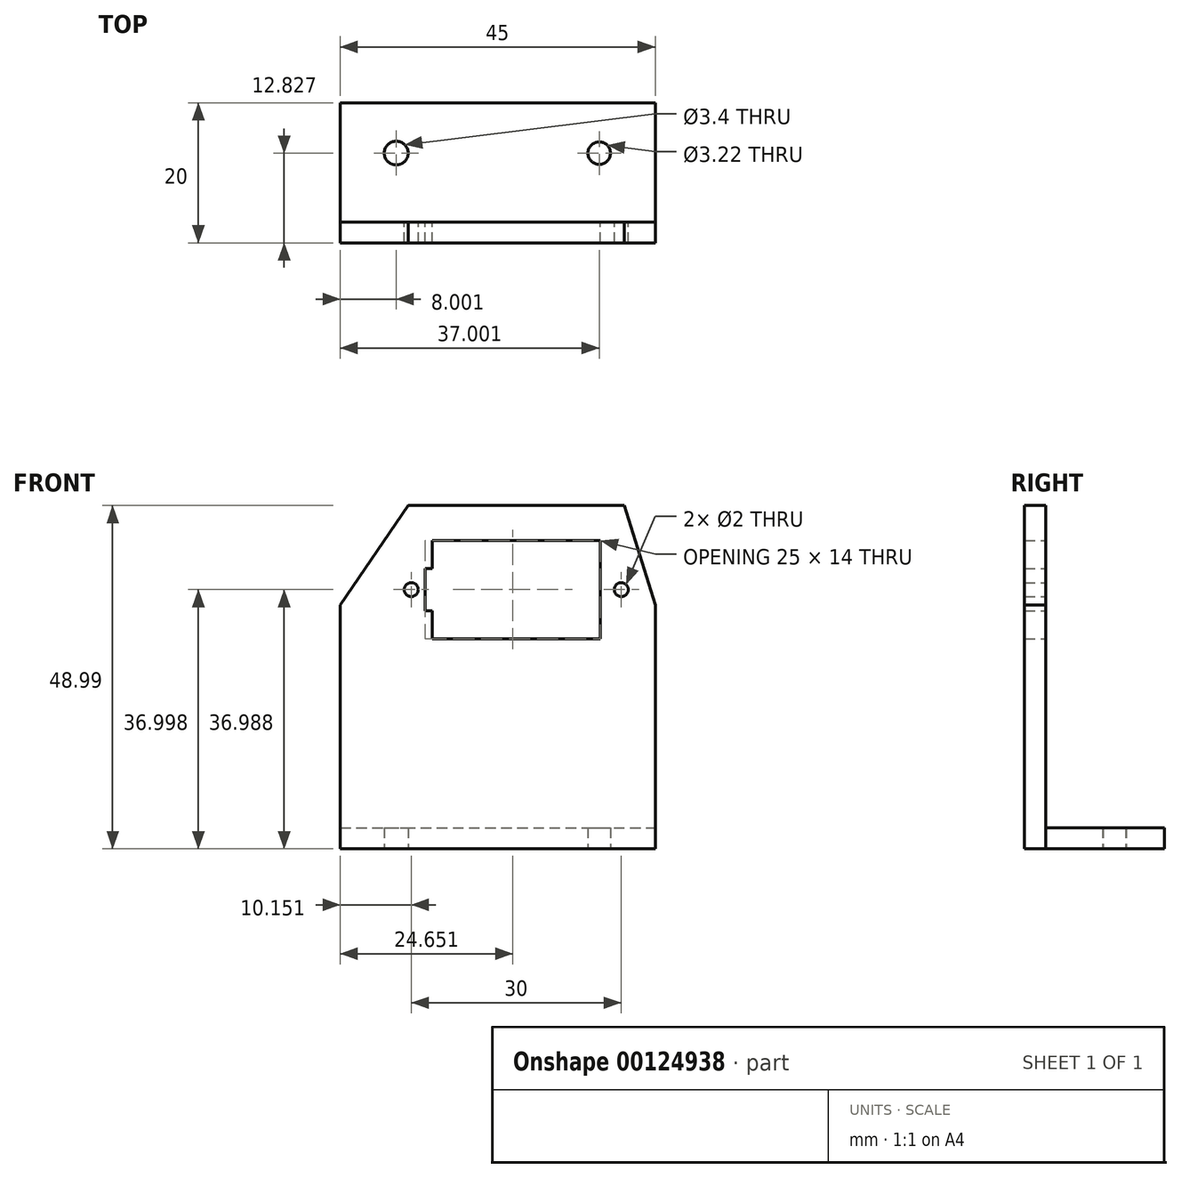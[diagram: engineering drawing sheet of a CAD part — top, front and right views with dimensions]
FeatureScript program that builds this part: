
annotation { "Feature Type Name" : "Feature", "Feature Type Description" : "" }
export const myFeature = defineFeature(function(context is Context, id is Id, definition is map)
    precondition{}
    {
        {
            var Q0;
            Q0=qCreatedBy(makeId("Front.planeOp"),FACE);
            var sketch = newSketch(context, id + "F0", { "sketchPlane" : qUnion([Q0])});
            skLineSegment(sketch, "E0.bottom", {"start": v(-32.87, 11.25) * mm, "end": v(-21.4, 10.36) * mm});
            skLineSegment(sketch, "E0.top", {"start": v(-33.29, 5.9) * mm, "end": v(-21.82, 5.01) * mm});
            skLineSegment(sketch, "E0.left", {"start": v(-32.87, 11.25) * mm, "end": v(-33.29, 5.9) * mm});
            skLineSegment(sketch, "E0.right", {"start": v(-21.4, 10.36) * mm, "end": v(-21.82, 5.01) * mm});
            skCircle(sketch, "E1", {"center": v(-36.58, 8.03) * mm, "radius": 1.23 * mm});
            skLineSegment(sketch, "E2", {"start": v(-21.5, 9.24) * mm, "end": v(-19.71, 9.1) * mm});
            skLineSegment(sketch, "E3", {"start": v(-19.71, 9.1) * mm, "end": v(-19.71, 7.18) * mm});
            skLineSegment(sketch, "E4", {"start": v(-19.71, 7.18) * mm, "end": v(-21.66, 7.09) * mm});
            skCircle(sketch, "E5", {"center": v(-17.91, 7.7) * mm, "radius": 1.15 * mm});
            skLineSegment(sketch, "E6", {"start": v(-37.07, 13.52) * mm, "end": v(-41.14, 9.38) * mm});
            skLineSegment(sketch, "E7", {"start": v(-41.14, 9.38) * mm, "end": v(-41.14, 1.17) * mm});
            skLineSegment(sketch, "E8", {"start": v(-41.14, 1.17) * mm, "end": v(-12.1, 1.17) * mm});
            skLineSegment(sketch, "E9", {"start": v(-12.1, 1.17) * mm, "end": v(-12.1, 9.38) * mm});
            skLineSegment(sketch, "E10", {"start": v(-12.1, 9.38) * mm, "end": v(-16.65, 13.45) * mm});
            skLineSegment(sketch, "E11", {"start": v(-16.65, 13.45) * mm, "end": v(-37.07, 13.52) * mm});
            skLineSegment(sketch, "E12.bottom", {"start": v(-51.3, -18.1) * mm, "end": v(-27.3, -18.1) * mm});
            skLineSegment(sketch, "E12.top", {"start": v(-51.3, -32.1) * mm, "end": v(-27.3, -32.1) * mm});
            skLineSegment(sketch, "E12.left", {"start": v(-51.3, -18.1) * mm, "end": v(-51.3, -32.1) * mm});
            skLineSegment(sketch, "E12.right", {"start": v(-27.3, -18.1) * mm, "end": v(-27.3, -32.1) * mm});
            skLineSegment(sketch, "E13", {"start": v(4.57, -32.1) * mm, "end": v(-59.19, -32.1) * mm, "construction": true});
            skCircle(sketch, "E14", {"center": v(-54.3, -25.1) * mm, "radius": 1 * mm});
            skCircle(sketch, "E15", {"center": v(-24.3, -25.1) * mm, "radius": 1 * mm});
            skPoint(sketch, "E16", {"position": v(-27.3, -25.1) * mm});
            skLineSegment(sketch, "E17", {"start": v(-61.71, -25.1) * mm, "end": v(7.1, -25.1) * mm, "construction": true});
            skLineSegment(sketch, "E18", {"start": v(-64.46, -62.1) * mm, "end": v(-19.46, -62.1) * mm});
            skLineSegment(sketch, "E19", {"start": v(-19.46, -62.1) * mm, "end": v(-19.46, -27.31) * mm});
            skLineSegment(sketch, "E20", {"start": v(-19.46, -27.31) * mm, "end": v(-23.89, -13.1) * mm});
            skLineSegment(sketch, "E21", {"start": v(-23.89, -13.1) * mm, "end": v(-54.73, -13.1) * mm});
            skLineSegment(sketch, "E22", {"start": v(-54.73, -13.1) * mm, "end": v(-64.46, -27.31) * mm});
            skLineSegment(sketch, "E23", {"start": v(-64.46, -27.31) * mm, "end": v(-64.46, -62.1) * mm});
            skPoint(sketch, "E24", {"position": v(-39.3, -32.1) * mm});
            skPoint(sketch, "E25", {"position": v(-39.3, -13.1) * mm});
            skLineSegment(sketch, "E26", {"start": v(-51.3, -22.1) * mm, "end": v(-52.3, -22.1) * mm});
            skLineSegment(sketch, "E27", {"start": v(-52.3, -22.1) * mm, "end": v(-52.3, -28.1) * mm});
            skLineSegment(sketch, "E28", {"start": v(-52.3, -28.1) * mm, "end": v(-51.3, -28.1) * mm});
            skPoint(sketch, "E29", {"position": v(-52.3, -25.1) * mm});
            skLineSegment(sketch, "E30.left", {"start": v(-19.46, -27.31) * mm, "end": v(-19.46, -60) * mm});
            skSolve(sketch);
        }
        {
            var Q0;
            {var subQ4=sQuery(id+"F0.wireOp",EDGE,"E12.bottom");Q0=makeQuery(id+"F0.imprint","IMPRINT",FACE,{"disambiguationData":[TD([[makeQuery(id+"F0.imprint","IMPRINT",EDGE,{"derivedFrom":subQ4}),1.0]])]});}
            extrude(context, id + "F1", {"entities" : qUnion([Q0]), "depth" : 3 * mm});
        }
        {
            var Q0;
            Q0=makeQuery(id+"F1.opExtrude","SWEPT_FACE",FACE,{"disambiguationData":[OSD([sQuery(id+"F0.wireOp",EDGE,"E18")])]});
            var sketch = newSketch(context, id + "F2", { "sketchPlane" : qUnion([Q0])});
            skLineSegment(sketch, "E31.bottom", {"start": v(-64.46, 3) * mm, "end": v(-19.46, 3) * mm});
            skLineSegment(sketch, "E31.top", {"start": v(-64.46, -17) * mm, "end": v(-19.46, -17) * mm});
            skLineSegment(sketch, "E31.left", {"start": v(-64.46, 3) * mm, "end": v(-64.46, -17) * mm});
            skLineSegment(sketch, "E31.right", {"start": v(-19.46, 3) * mm, "end": v(-19.46, -17) * mm});
            skCircle(sketch, "E32", {"center": v(-56.46, -9.83) * mm, "radius": 1.7 * mm});
            skCircle(sketch, "E33", {"center": v(-27.46, -9.83) * mm, "radius": 1.61 * mm});
            skPoint(sketch, "E34", {"position": v(-64.46, -7) * mm});
            skSolve(sketch);
        }
        {
            var Q0;
            {var subQ2=sQuery(id+"F2.wireOp",EDGE,"E31.top");Q0=makeQuery(id+"F2.imprint","IMPRINT",FACE,{"disambiguationData":[TD([[makeQuery(id+"F2.imprint","IMPRINT",EDGE,{"derivedFrom":subQ2}),1.0]])]});}
            extrude(context, id + "F3", {"entities" : qUnion([Q0]), "oppositeDirection" : true, "depth" : 3 * mm});
        }
    });
